# Revit family: Hager-GOLF-Surface_mounted-IP40-With_Cover-With_DIN-NoHosted-PT-pt
name_source: partatom
category: Electrical Equipment
units: mm (PartAtom-declared; Revit-internal decimal feet)

## family parameters
Always vertical = Yes
Cut with Voids When Loaded = No
Maintain Annotation Orientation = No
Panel Configuration = Two Columns, Circuits Across
Part Type = Panelboard
Room Calculation Point = No
Round Connector Dimension = Use Diameter
Shared = No
Work Plane-Based = Yes

## types (22) — shared parameters
Code hager = ADD-EC000214_EU
Default Elevation = 1200 mm
EF000003 - Método de montaje = Surface mounted
EF000007 - Color = White
EF000024 - Resistente a UV = No
EF000049 - Profundidad = 99 mm  [stored 0.324803 ft]
EF000116 - Número RAL = 9010
EF000118 - Con placa de montaje = No
EF001062 - Versión de CEM = No
EF001088 - Posibilidad de extensión = Yes
EF001134 - Carril DIN = Yes
EF004462 - Tipo de cierre = Other
EF005474 - Grado de protección (IP) = IP40
EF006306 - Con candado = No
EF009212 - Versión de la cubierta = Closed
EF015776 - Borne de tierra = Yes
EF015777 - Borne neutro = Yes
EF015941 - Puerta de transmisión de señal = Yes
ETIM class code = EC000214
ETIM class name = Small distribution board
HG000001-Number of columns = 1
HG000002-With door or cover = Yes
HG000003-Range = GOLF
HG000005-Thickness = 2 mm  [stored 0.00656168 ft]
HG000006-Flush mounted = No
HG000009-Double swing door = No
HG000010-Asymmetric doors = No
HG000011-Empty rows from bottom = No
HG000012-Door swing angle = 90.00°
HG000013-Door on the left = No
HG000014-Door on the right = Yes
HG000015-Clearance visibility = Yes
HG000016-Door 3D visibility = Yes
HG000017-Distance between poles = 18 mm  [stored 0.0590551 ft]
HG000060-RAL-number = 9010
HG000099-Onfly Template ID = 507532
Manufacturer = Hager
Name BIM&CO = Electricity
Name hager = ADD_Enclosures_EC000214
Reference = Template-Enclosure_EU-EC000214
Uniformat = Low Tension Service & Dist.
Uniformat code = D501001
zero-valued in all types: EF000218 - Profundidad de instalación, EF000332 - Altura de la instalación, EF000846 - Anchura de montaje, EF001131 - Profundidad interna, HG000007-Number of empty columns, HG000008-Number of empty rows

## per-type parameters (varying)
| type | BC_METADATA | EF000008 - Anchura | EF000040 - Altura | EF000266 - Número de filas | EF002950 - Ancho en número de espacios modulares | EF006244 - Tapa/puerta transparente | HG000004-Manufacturer reference | HGEF000266-Number of rows | HGEF002950-Width in number of modular spacings |
| GOLF-Surface_mounted_W138_H184_D99_4_Modular_Spacing-VS104PP | {"ObjectGuid":"848913b6-0210-4ab5-a193-952b96a552a7","ModelGuid":"9ded9e48-f739-4a4f-aa7c-cd040b74238b","VariantGuid":"fca866d6-de43-4ca1-9124-c5785c1da926","Revision":"#3","VariantName":"GOLF-Surface_mounted_W138_H184_D99_4_Modular_Spacing-VS104PP"} | 138 mm  [stored 0.452756 ft] | 184 mm  [stored 0.603675 ft] | 1 | 4 | No | VS104PP | 1 | 4 |
| GOLF-Surface_mounted_W138_H184_D99_4_Modular_Spacing-VS104TP | {"ObjectGuid":"848913b6-0210-4ab5-a193-952b96a552a7","ModelGuid":"9ded9e48-f739-4a4f-aa7c-cd040b74238b","VariantGuid":"567adb54-ae81-401d-9a48-7af8cf2fee67","Revision":"#3","VariantName":"GOLF-Surface_mounted_W138_H184_D99_4_Modular_Spacing-VS104TP"} | 138 mm  [stored 0.452756 ft] | 184 mm  [stored 0.603675 ft] | 1 | 4 | Yes | VS104TP | 1 | 4 |
| GOLF-Surface_mounted_W210_H184_D99_8_Modular_Spacing-VS108PP | {"ObjectGuid":"848913b6-0210-4ab5-a193-952b96a552a7","ModelGuid":"9ded9e48-f739-4a4f-aa7c-cd040b74238b","VariantGuid":"6e3f202d-4ff0-4b3c-8858-e999ea530c8c","Revision":"#3","VariantName":"GOLF-Surface_mounted_W210_H184_D99_8_Modular_Spacing-VS108PP"} | 210 mm | 184 mm  [stored 0.603675 ft] | 1 | 8 | No | VS108PP | 1 | 8 |
| GOLF-Surface_mounted_W210_H184_D99_8_Modular_Spacing-VS108TP | {"ObjectGuid":"848913b6-0210-4ab5-a193-952b96a552a7","ModelGuid":"9ded9e48-f739-4a4f-aa7c-cd040b74238b","VariantGuid":"d09e042c-e15b-4b64-9b88-51b7451012c8","Revision":"#3","VariantName":"GOLF-Surface_mounted_W210_H184_D99_8_Modular_Spacing-VS108TP"} | 210 mm | 184 mm  [stored 0.603675 ft] | 1 | 8 | Yes | VS108TP | 1 | 8 |
| GOLF-Surface_mounted_W282_H252_D99_12_Modular_Spacing-VS112PP | {"ObjectGuid":"848913b6-0210-4ab5-a193-952b96a552a7","ModelGuid":"9ded9e48-f739-4a4f-aa7c-cd040b74238b","VariantGuid":"5d606a16-01e4-4ab6-b559-ffec1f95544e","Revision":"#3","VariantName":"GOLF-Surface_mounted_W282_H252_D99_12_Modular_Spacing-VS112PP"} | 282 mm | 252 mm | 1 | 12 | No | VS112PP | 1 | 12 |
| GOLF-Surface_mounted_W282_H252_D99_12_Modular_Spacing-VS112TP | {"ObjectGuid":"848913b6-0210-4ab5-a193-952b96a552a7","ModelGuid":"9ded9e48-f739-4a4f-aa7c-cd040b74238b","VariantGuid":"dba8fb12-68f2-42d4-8956-2c886d996625","Revision":"#3","VariantName":"GOLF-Surface_mounted_W282_H252_D99_12_Modular_Spacing-VS112TP"} | 282 mm | 252 mm | 1 | 12 | Yes | VS112TP | 1 | 12 |
| GOLF-Surface_mounted_W390_H252_D99_18_Modular_Spacing-VS118PP | {"ObjectGuid":"848913b6-0210-4ab5-a193-952b96a552a7","ModelGuid":"9ded9e48-f739-4a4f-aa7c-cd040b74238b","VariantGuid":"f1956a20-3563-42d9-a3f0-c06e36e26654","Revision":"#3","VariantName":"GOLF-Surface_mounted_W390_H252_D99_18_Modular_Spacing-VS118PP"} | 390 mm | 252 mm | 1 | 18 | No | VS118PP | 1 | 18 |
| GOLF-Surface_mounted_W390_H252_D99_18_Modular_Spacing-VS118TP | {"ObjectGuid":"848913b6-0210-4ab5-a193-952b96a552a7","ModelGuid":"9ded9e48-f739-4a4f-aa7c-cd040b74238b","VariantGuid":"97f54356-c5b4-4950-a0dd-709192a3596f","Revision":"#3","VariantName":"GOLF-Surface_mounted_W390_H252_D99_18_Modular_Spacing-VS118TP"} | 390 mm | 252 mm | 1 | 18 | Yes | VS118TP | 1 | 18 |
| GOLF-Surface_mounted_W462_H252_D99_22_Modular_Spacing-VS122PP | {"ObjectGuid":"848913b6-0210-4ab5-a193-952b96a552a7","ModelGuid":"9ded9e48-f739-4a4f-aa7c-cd040b74238b","VariantGuid":"dd5383ec-dbab-413c-925a-1fdf07f4e0a0","Revision":"#3","VariantName":"GOLF-Surface_mounted_W462_H252_D99_22_Modular_Spacing-VS122PP"} | 462 mm | 252 mm | 1 | 22 | No | VS122PP | 1 | 22 |
| GOLF-Surface_mounted_W462_H252_D99_22_Modular_Spacing-VS122TP | {"ObjectGuid":"848913b6-0210-4ab5-a193-952b96a552a7","ModelGuid":"9ded9e48-f739-4a4f-aa7c-cd040b74238b","VariantGuid":"8d456a3e-3393-4bb4-99de-643614b8aaaa","Revision":"#3","VariantName":"GOLF-Surface_mounted_W462_H252_D99_22_Modular_Spacing-VS122TP"} | 462 mm | 252 mm | 1 | 22 | Yes | VS122TP | 1 | 22 |
| GOLF-Surface_mounted_W282_H377_D99_12_Modular_Spacing-VS212PP | {"ObjectGuid":"848913b6-0210-4ab5-a193-952b96a552a7","ModelGuid":"9ded9e48-f739-4a4f-aa7c-cd040b74238b","VariantGuid":"a762af3b-3aac-4178-89e8-4f469cd134ce","Revision":"#3","VariantName":"GOLF-Surface_mounted_W282_H377_D99_12_Modular_Spacing-VS212PP"} | 282 mm | 377 mm | 2 | 12 | No | VS212PP | 2 | 12 |
| GOLF-Surface_mounted_W282_H377_D99_12_Modular_Spacing-VS212TP | {"ObjectGuid":"848913b6-0210-4ab5-a193-952b96a552a7","ModelGuid":"9ded9e48-f739-4a4f-aa7c-cd040b74238b","VariantGuid":"6f4beff4-5ac9-4510-a099-6f6c79cc864b","Revision":"#3","VariantName":"GOLF-Surface_mounted_W282_H377_D99_12_Modular_Spacing-VS212TP"} | 282 mm | 377 mm | 2 | 12 | Yes | VS212TP | 2 | 12 |
| GOLF-Surface_mounted_W390_H377_D99_18_Modular_Spacing-VS218PP | {"ObjectGuid":"848913b6-0210-4ab5-a193-952b96a552a7","ModelGuid":"9ded9e48-f739-4a4f-aa7c-cd040b74238b","VariantGuid":"13eb9557-a1c3-4b2d-8f53-1fa8df3f562b","Revision":"#3","VariantName":"GOLF-Surface_mounted_W390_H377_D99_18_Modular_Spacing-VS218PP"} | 390 mm | 377 mm | 2 | 18 | No | VS218PP | 2 | 18 |
| GOLF-Surface_mounted_W390_H377_D99_18_Modular_Spacing-VS218TP | {"ObjectGuid":"848913b6-0210-4ab5-a193-952b96a552a7","ModelGuid":"9ded9e48-f739-4a4f-aa7c-cd040b74238b","VariantGuid":"1d216d8b-f8bf-46a0-83ff-6575f4599c82","Revision":"#3","VariantName":"GOLF-Surface_mounted_W390_H377_D99_18_Modular_Spacing-VS218TP"} | 390 mm | 377 mm | 2 | 18 | Yes | VS218TP | 2 | 18 |
| GOLF-Surface_mounted_W282_H500_D99_12_Modular_Spacing-VS312PP | {"ObjectGuid":"848913b6-0210-4ab5-a193-952b96a552a7","ModelGuid":"9ded9e48-f739-4a4f-aa7c-cd040b74238b","VariantGuid":"02507c2a-cfc0-403b-896c-cb1f2450231b","Revision":"#3","VariantName":"GOLF-Surface_mounted_W282_H500_D99_12_Modular_Spacing-VS312PP"} | 282 mm | 500 mm  [stored 1.64042 ft] | 3 | 12 | No | VS312PP | 3 | 12 |
| GOLF-Surface_mounted_W282_H500_D99_12_Modular_Spacing-VS312TP | {"ObjectGuid":"848913b6-0210-4ab5-a193-952b96a552a7","ModelGuid":"9ded9e48-f739-4a4f-aa7c-cd040b74238b","VariantGuid":"c8407b54-2fe5-457e-95d7-e21ba1ceb42c","Revision":"#3","VariantName":"GOLF-Surface_mounted_W282_H500_D99_12_Modular_Spacing-VS312TP"} | 282 mm | 500 mm  [stored 1.64042 ft] | 3 | 12 | Yes | VS312TP | 3 | 12 |
| GOLF-Surface_mounted_W390_H500_D99_18_Modular_Spacing-VS318PP | {"ObjectGuid":"848913b6-0210-4ab5-a193-952b96a552a7","ModelGuid":"9ded9e48-f739-4a4f-aa7c-cd040b74238b","VariantGuid":"64e84b48-7b33-46a7-9085-e901ff734a19","Revision":"#3","VariantName":"GOLF-Surface_mounted_W390_H500_D99_18_Modular_Spacing-VS318PP"} | 390 mm | 500 mm  [stored 1.64042 ft] | 3 | 18 | No | VS318PP | 3 | 18 |
| GOLF-Surface_mounted_W390_H500_D99_18_Modular_Spacing-VS318TP | {"ObjectGuid":"848913b6-0210-4ab5-a193-952b96a552a7","ModelGuid":"9ded9e48-f739-4a4f-aa7c-cd040b74238b","VariantGuid":"c9e8582c-ed81-441e-812b-2df1aff4882a","Revision":"#3","VariantName":"GOLF-Surface_mounted_W390_H500_D99_18_Modular_Spacing-VS318TP"} | 390 mm | 500 mm  [stored 1.64042 ft] | 3 | 18 | Yes | VS318TP | 3 | 18 |
| GOLF-Surface_mounted_W282_H647_D99_12_Modular_Spacing-VS412PP | {"ObjectGuid":"848913b6-0210-4ab5-a193-952b96a552a7","ModelGuid":"9ded9e48-f739-4a4f-aa7c-cd040b74238b","VariantGuid":"13b54c44-195a-4b49-bb81-9a9548a467c7","Revision":"#3","VariantName":"GOLF-Surface_mounted_W282_H647_D99_12_Modular_Spacing-VS412PP"} | 282 mm | 647 mm | 4 | 12 | No | VS412PP | 4 | 12 |
| GOLF-Surface_mounted_W282_H647_D99_12_Modular_Spacing-VS412TP | {"ObjectGuid":"848913b6-0210-4ab5-a193-952b96a552a7","ModelGuid":"9ded9e48-f739-4a4f-aa7c-cd040b74238b","VariantGuid":"a34bd198-861a-4ea1-9948-eb9cf3c8bb8e","Revision":"#3","VariantName":"GOLF-Surface_mounted_W282_H647_D99_12_Modular_Spacing-VS412TP"} | 282 mm | 647 mm | 4 | 12 | Yes | VS412TP | 4 | 12 |
| GOLF-Surface_mounted_W390_H647_D99_18_Modular_Spacing-VS418PP | {"ObjectGuid":"848913b6-0210-4ab5-a193-952b96a552a7","ModelGuid":"9ded9e48-f739-4a4f-aa7c-cd040b74238b","VariantGuid":"e09ea683-5051-4848-b5f0-9de9da202e36","Revision":"#3","VariantName":"GOLF-Surface_mounted_W390_H647_D99_18_Modular_Spacing-VS418PP"} | 390 mm | 647 mm | 4 | 18 | No | VS418PP | 4 | 18 |
| GOLF-Surface_mounted_W390_H647_D99_18_Modular_Spacing-VS418TP | {"ObjectGuid":"848913b6-0210-4ab5-a193-952b96a552a7","ModelGuid":"9ded9e48-f739-4a4f-aa7c-cd040b74238b","VariantGuid":"f1b5d54a-e727-49b8-816b-3e455941d9f8","Revision":"#3","VariantName":"GOLF-Surface_mounted_W390_H647_D99_18_Modular_Spacing-VS418TP"} | 390 mm | 647 mm | 4 | 18 | Yes | VS418TP | 4 | 18 |

note: [stored X ft] marks values corroborated as IEEE doubles in the binary element streams (Revit-internal decimal feet)

## geometry (parser evidence)
native form markers: Sweep x13
no freeform markers — native parametric forms only
